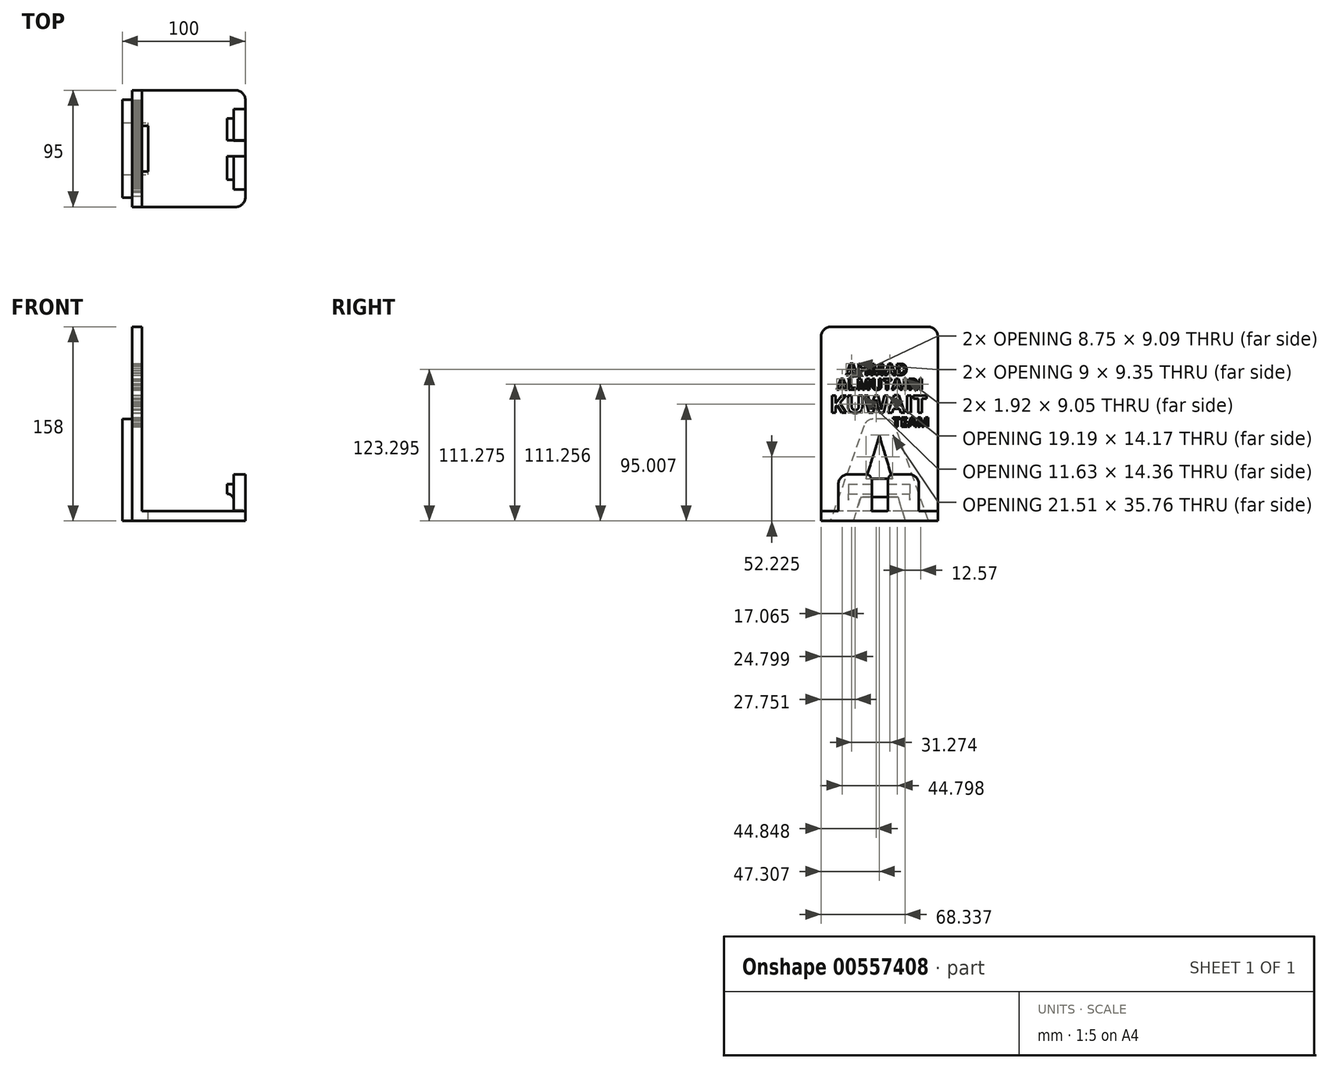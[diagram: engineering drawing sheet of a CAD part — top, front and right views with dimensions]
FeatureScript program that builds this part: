
annotation { "Feature Type Name" : "Feature", "Feature Type Description" : "" }
export const myFeature = defineFeature(function(context is Context, id is Id, definition is map)
    precondition{}
    {
        {
            var Q0;
            Q0=qCreatedBy(makeId("Top.planeOp"),FACE);
            var sketch = newSketch(context, id + "F0", { "sketchPlane" : qUnion([Q0])});
            skLineSegment(sketch, "E0.bottom", {"start": v(-46, -47.5) * mm, "end": v(46, -47.5) * mm});
            skLineSegment(sketch, "E0.top", {"start": v(-46, 47.5) * mm, "end": v(46, 47.5) * mm});
            skLineSegment(sketch, "E0.left", {"start": v(-46, -47.5) * mm, "end": v(-46, 47.5) * mm});
            skLineSegment(sketch, "E0.right", {"start": v(46, -47.5) * mm, "end": v(46, 47.5) * mm});
            skPoint(sketch, "E0.middle", {"position": v(0, 0) * mm});
            skSolve(sketch);
        }
        {
            var Q0;
            Q0=makeQuery(id+"F0.imprint","IMPRINT",FACE,{"disambiguationData":[TD([[makeQuery(id+"F0.imprint","IMPRINT",EDGE,{"derivedFrom":sQuery(id+"F0.wireOp",EDGE,"E0.bottom")}),1.0]])]});
            extrude(context, id + "F1", {"entities" : qUnion([Q0]), "depth" : 8 * mm, "offsetDistance" : 25 * mm});
        }
        {
            var Q0;
            Q0=makeQuery(id+"F1.opExtrude","CAP_FACE",FACE,{"disambiguationData":[OSD([sQuery(id+"F0.wireOp",EDGE,"E0.bottom"),sQuery(id+"F0.wireOp",EDGE,"E0.top"),sQuery(id+"F0.wireOp",EDGE,"E0.left"),sQuery(id+"F0.wireOp",EDGE,"E0.right")])],"isStart":false});
            var sketch = newSketch(context, id + "F2", { "sketchPlane" : qUnion([Q0])});
            skLineSegment(sketch, "E1.bottom", {"start": v(-46, 47.5) * mm, "end": v(-38, 47.5) * mm});
            skLineSegment(sketch, "E1.top", {"start": v(-46, -47.5) * mm, "end": v(-38, -47.5) * mm});
            skLineSegment(sketch, "E1.left", {"start": v(-46, 47.5) * mm, "end": v(-46, -47.5) * mm});
            skLineSegment(sketch, "E1.right", {"start": v(-38, 47.5) * mm, "end": v(-38, -47.5) * mm});
            skSolve(sketch);
        }
        {
            var Q0;
            Q0=qSketchRegion(id+"F2",true);
            extrude(context, id + "F3", {"entities" : qUnion([Q0]), "operationType" : NewBodyOperationType.ADD, "depth" : 150 * mm, "offsetDistance" : 25 * mm});
        }
        {
            var Q0;
            Q0=makeQuery(id+"F1.opExtrude","CAP_FACE",FACE,{"disambiguationData":[OSD([sQuery(id+"F0.wireOp",EDGE,"E0.bottom"),sQuery(id+"F0.wireOp",EDGE,"E0.top"),sQuery(id+"F0.wireOp",EDGE,"E0.left"),sQuery(id+"F0.wireOp",EDGE,"E0.right")])],"isStart":false});
            var sketch = newSketch(context, id + "F4", { "sketchPlane" : qUnion([Q0])});
            skLineSegment(sketch, "E2.bottom", {"start": v(46, 32.06) * mm, "end": v(36.5, 32.06) * mm});
            skLineSegment(sketch, "E2.top", {"start": v(46, -33.37) * mm, "end": v(36.5, -33.37) * mm});
            skLineSegment(sketch, "E2.left", {"start": v(46, 32.06) * mm, "end": v(46, -33.37) * mm});
            skLineSegment(sketch, "E2.right", {"start": v(36.5, 32.06) * mm, "end": v(36.5, -33.37) * mm});
            skSolve(sketch);
        }
        {
            var Q0;
            Q0=makeQuery(id+"F4.imprint","IMPRINT",FACE,{"disambiguationData":[TD([[makeQuery(id+"F4.imprint","IMPRINT",EDGE,{"derivedFrom":sQuery(id+"F4.wireOp",EDGE,"E2.bottom")}),1.0]])]});
            extrude(context, id + "F5", {"entities" : qUnion([Q0]), "operationType" : NewBodyOperationType.ADD, "depth" : 30 * mm, "offsetDistance" : 25 * mm});
        }
        {
            var Q0;
            Q0=makeQuery(id+"F3.boolean.opBoolean","MERGE",FACE,{"derivedFrom":[makeQuery(id+"F1.opExtrude","SWEPT_FACE",FACE,{"disambiguationData":[OSD([sQuery(id+"F0.wireOp",EDGE,"E0.left")])]}),makeQuery(id+"F3.opExtrude","SWEPT_FACE",FACE,{"disambiguationData":[OSD([sQuery(id+"F2.wireOp",EDGE,"E1.left")])]})]});
            var sketch = newSketch(context, id + "F6", { "sketchPlane" : qUnion([Q0])});
            skText(sketch, "E3", { "text": "A", "fontName": "OpenSans-Bold.ttf"});
            const initialGuessF6  = {"E3": [-0.03983, 0, 1, 0, 0.0833]};
            skSetInitialGuess(sketch, initialGuessF6);
            skSolve(sketch);
        }
        {
            var Q0;
            Q0=qSketchRegion(id+"F6",true);
            extrude(context, id + "F7", {"entities" : qUnion([Q0]), "operationType" : NewBodyOperationType.ADD, "depth" : 8 * mm, "offsetDistance" : 25 * mm});
        }
        {
            var Q0;
            Q0=makeQuery(id+"F7.boolean.opBoolean","SPLIT",FACE,{"disambiguationData":[TD([makeQuery(id+"F7.opExtrude","SWEPT_FACE",FACE,{"disambiguationData":[OSD([sQuery(id+"F6.wireOp",EDGE,"E3.sketch_text.stroke-8")])]})])],"derivedFrom":makeQuery(id+"F3.boolean.opBoolean","MERGE",FACE,{"derivedFrom":[makeQuery(id+"F1.opExtrude","SWEPT_FACE",FACE,{"disambiguationData":[OSD([sQuery(id+"F0.wireOp",EDGE,"E0.left")])]}),makeQuery(id+"F3.opExtrude","SWEPT_FACE",FACE,{"disambiguationData":[OSD([sQuery(id+"F2.wireOp",EDGE,"E1.left")])]})]})});
            var Q1;
            {var subQ0=sQuery(id+"F0.wireOp",EDGE,"E0.left");Q1=makeQuery(id+"F7.boolean.opBoolean","SPLIT",FACE,{"disambiguationData":[TD([makeQuery(id+"F7.opExtrude","SWEPT_FACE",FACE,{"disambiguationData":[OSD([sQuery(id+"F6.wireOp",EDGE,"E3.sketch_text.stroke-0")])]})])],"derivedFrom":makeQuery(id+"F3.boolean.opBoolean","MERGE",FACE,{"derivedFrom":[makeQuery(id+"F1.opExtrude","SWEPT_FACE",FACE,{"disambiguationData":[OSD([subQ0])]}),makeQuery(id+"F3.opExtrude","SWEPT_FACE",FACE,{"disambiguationData":[OSD([sQuery(id+"F2.wireOp",EDGE,"E1.left")])]})]})});}
            extrude(context, id + "F8", {"entities" : qUnion([Q0, Q1]), "operationType" : NewBodyOperationType.REMOVE, "oppositeDirection" : true, "depth" : 13 * mm, "offsetDistance" : 25 * mm});
        }
        {
            var Q0;
            Q0=makeQuery(id+"F1.opExtrude","CAP_FACE",FACE,{"disambiguationData":[OSD([sQuery(id+"F0.wireOp",EDGE,"E0.bottom"),sQuery(id+"F0.wireOp",EDGE,"E0.top"),sQuery(id+"F0.wireOp",EDGE,"E0.left"),sQuery(id+"F0.wireOp",EDGE,"E0.right")])],"isStart":false});
            var sketch = newSketch(context, id + "F9", { "sketchPlane" : qUnion([Q0])});
            skLineSegment(sketch, "E4.bottom", {"start": v(-46.36, -6.41) * mm, "end": v(46.36, -6.41) * mm});
            skLineSegment(sketch, "E4.top", {"start": v(-46.36, 6.41) * mm, "end": v(46.36, 6.41) * mm});
            skLineSegment(sketch, "E4.left", {"start": v(-46.36, -6.41) * mm, "end": v(-46.36, 6.41) * mm});
            skLineSegment(sketch, "E4.right", {"start": v(46.36, -6.41) * mm, "end": v(46.36, 6.41) * mm});
            skPoint(sketch, "E4.middle", {"position": v(0, 0) * mm});
            skSolve(sketch);
        }
        {
            var Q0;
            Q0=qSketchRegion(id+"F9",true);
            extrude(context, id + "F10", {"entities" : qUnion([Q0]), "operationType" : NewBodyOperationType.REMOVE, "depth" : 8 * mm, "offsetDistance" : 25 * mm});
        }
        {
            var Q0;
            Q0=makeQuery(id+"F5.opExtrude","CAP_EDGE",EDGE,{"disambiguationData":[OSD([sQuery(id+"F4.wireOp",EDGE,"E2.top")])],"isStart":false});
            var Q1;
            Q1=makeQuery(id+"F10.boolean.opBoolean","COPY",EDGE,{"derivedFrom":makeQuery(id+"F10.opExtrude","CAP_EDGE",EDGE,{"disambiguationData":[OSD([sQuery(id+"F9.wireOp",EDGE,"E4.bottom")])],"isStart":false})});
            var Q2;
            Q2=makeQuery(id+"F5.opExtrude","CAP_EDGE",EDGE,{"disambiguationData":[OSD([sQuery(id+"F4.wireOp",EDGE,"E2.bottom")])],"isStart":false});
            var Q3;
            Q3=makeQuery(id+"F10.boolean.opBoolean","COPY",EDGE,{"derivedFrom":makeQuery(id+"F10.opExtrude","CAP_EDGE",EDGE,{"disambiguationData":[OSD([sQuery(id+"F9.wireOp",EDGE,"E4.top")])],"isStart":false})});
            var Q4;
            Q4=makeQuery(id+"F1.opExtrude","SWEPT_EDGE",EDGE,{"disambiguationData":[OSD([sQuery(id+"F0.wireOp",EDGE,"E0.bottom"),sQuery(id+"F0.wireOp",EDGE,"E0.right")])]});
            var Q5;
            Q5=makeQuery(id+"F1.opExtrude","SWEPT_EDGE",EDGE,{"disambiguationData":[OSD([sQuery(id+"F0.wireOp",EDGE,"E0.top"),sQuery(id+"F0.wireOp",EDGE,"E0.right")])]});
            var Q6;
            Q6=makeQuery(id+"F3.opExtrude","CAP_EDGE",EDGE,{"disambiguationData":[OSD([sQuery(id+"F2.wireOp",EDGE,"E1.bottom")])],"isStart":false});
            var Q7;
            Q7=makeQuery(id+"F3.opExtrude","CAP_EDGE",EDGE,{"disambiguationData":[OSD([sQuery(id+"F2.wireOp",EDGE,"E1.top")])],"isStart":false});
            var Q8;
            Q8=makeQuery(id+"F7.opExtrude","SWEPT_EDGE",EDGE,{"disambiguationData":[OSD([sQuery(id+"F6.wireOp",EDGE,"E3.sketch_text.stroke-5"),sQuery(id+"F6.wireOp",EDGE,"E3.sketch_text.stroke-6")])]});
            var Q9;
            Q9=makeQuery(id+"F7.opExtrude","SWEPT_EDGE",EDGE,{"disambiguationData":[OSD([sQuery(id+"F6.wireOp",EDGE,"E3.sketch_text.stroke-4"),sQuery(id+"F6.wireOp",EDGE,"E3.sketch_text.stroke-5")])]});
            fillet(context, id + "F11", {"entities" : qUnion([Q0, Q1, Q2, Q3, Q4, Q5, Q6, Q7, Q8, Q9]), "radius" : 8 * mm, "tangentPropagation" : true, "allowEdgeOverflow" : false});
        }
        {
            var Q0;
            Q0=makeQuery(id+"F3.opExtrude","SWEPT_FACE",FACE,{"disambiguationData":[OSD([sQuery(id+"F2.wireOp",EDGE,"E1.right")])]});
            var sketch = newSketch(context, id + "F12", { "sketchPlane" : qUnion([Q0])});
            skSolve(sketch);
        }
        {
            var Q0;
            Q0=makeQuery(id+"F5.boolean.opBoolean","MERGE",FACE,{"derivedFrom":[makeQuery(id+"F1.opExtrude","SWEPT_FACE",FACE,{"disambiguationData":[OSD([sQuery(id+"F0.wireOp",EDGE,"E0.right")])]}),makeQuery(id+"F5.opExtrude","SWEPT_FACE",FACE,{"disambiguationData":[OSD([sQuery(id+"F4.wireOp",EDGE,"E2.left")])]})]});
            var sketch = newSketch(context, id + "F13", { "sketchPlane" : qUnion([Q0])});
            skLineSegment(sketch, "E5.bottom", {"start": v(-25.37, 30) * mm, "end": v(24.63, 30) * mm});
            skLineSegment(sketch, "E5.top", {"start": v(-25.37, 22) * mm, "end": v(24.63, 22) * mm});
            skLineSegment(sketch, "E5.left", {"start": v(-25.37, 30) * mm, "end": v(-25.37, 22) * mm});
            skLineSegment(sketch, "E5.right", {"start": v(24.63, 30) * mm, "end": v(24.63, 22) * mm});
            skSolve(sketch);
        }
        {
            var Q0;
            Q0=qSketchRegion(id+"F13",true);
            extrude(context, id + "F14", {"entities" : qUnion([Q0]), "operationType" : NewBodyOperationType.ADD, "oppositeDirection" : true, "depth" : 15 * mm, "offsetDistance" : 25 * mm});
        }
        {
            var Q0;
            Q0=qCreatedBy(makeId("Right.planeOp"),FACE);
            var sketch = newSketch(context, id + "F15", { "sketchPlane" : qUnion([Q0])});
            skLineSegment(sketch, "E6.bottom", {"start": v(-6.29, 8.45) * mm, "end": v(6.71, 8.45) * mm});
            skLineSegment(sketch, "E6.top", {"start": v(-6.29, 38.45) * mm, "end": v(6.71, 38.45) * mm});
            skLineSegment(sketch, "E6.left", {"start": v(-6.29, 8.45) * mm, "end": v(-6.29, 38.45) * mm});
            skLineSegment(sketch, "E6.right", {"start": v(6.71, 8.45) * mm, "end": v(6.71, 38.45) * mm});
            skSolve(sketch);
        }
        {
            var Q0;
            Q0=qSketchRegion(id+"F15",true);
            extrude(context, id + "F16", {"entities" : qUnion([Q0]), "operationType" : NewBodyOperationType.REMOVE, "depth" : 51 * mm, "offsetDistance" : 25 * mm});
        }
        {
            var Q0;
            Q0=makeQuery(id+"F16.boolean.opBoolean","INTERSECT",EDGE,{"derivedFrom":[makeQuery(id+"F5.opExtrude","CAP_FACE",FACE,{"disambiguationData":[OSD([sQuery(id+"F4.wireOp",EDGE,"E2.bottom"),sQuery(id+"F4.wireOp",EDGE,"E2.top"),sQuery(id+"F4.wireOp",EDGE,"E2.left"),sQuery(id+"F4.wireOp",EDGE,"E2.right")])],"isStart":false}),makeQuery(id+"F16.opExtrude","SWEPT_FACE",FACE,{"disambiguationData":[OSD([sQuery(id+"F15.wireOp",EDGE,"E6.left")])]})]});
            var Q1;
            Q1=makeQuery(id+"F16.boolean.opBoolean","INTERSECT",EDGE,{"derivedFrom":[makeQuery(id+"F5.opExtrude","CAP_FACE",FACE,{"disambiguationData":[OSD([sQuery(id+"F4.wireOp",EDGE,"E2.bottom"),sQuery(id+"F4.wireOp",EDGE,"E2.top"),sQuery(id+"F4.wireOp",EDGE,"E2.left"),sQuery(id+"F4.wireOp",EDGE,"E2.right")])],"isStart":false}),makeQuery(id+"F16.opExtrude","SWEPT_FACE",FACE,{"disambiguationData":[OSD([sQuery(id+"F15.wireOp",EDGE,"E6.right")])]})]});
            fillet(context, id + "F17", {"entities" : qUnion([Q0, Q1]), "radius" : 5 * mm, "tangentPropagation" : true, "allowEdgeOverflow" : false});
        }
        {
            var Q0;
            {var subQ0=sQuery(id+"F2.wireOp",EDGE,"E1.right");Q0=makeQuery(id+"F12.imprint","IMPRINT",FACE,{"disambiguationData":[TD([[makeQuery(id+"F12.imprint","IMPRINT",EDGE,{"derivedFrom":makeQuery(id+"F3.opExtrude","CAP_EDGE",EDGE,{"disambiguationData":[OSD([subQ0])],"isStart":false})}),1.0]])]});}
            var sketch = newSketch(context, id + "F18", { "sketchPlane" : qUnion([Q0])});
            skText(sketch, "E7", { "text": "KUWAIT", "fontName": "OpenSans-Bold.ttf"});
            const initialGuessF18  = {"E7": [-0.04043, 0.08802, 1, 0, 0.01429]};
            skSetInitialGuess(sketch, initialGuessF18);
            skSolve(sketch);
        }
        {
            var Q0;
            {var subQ0=sQuery(id+"F2.wireOp",EDGE,"E1.right");Q0=makeQuery(id+"F12.imprint","IMPRINT",FACE,{"disambiguationData":[TD([[makeQuery(id+"F12.imprint","IMPRINT",EDGE,{"derivedFrom":makeQuery(id+"F3.opExtrude","CAP_EDGE",EDGE,{"disambiguationData":[OSD([subQ0])],"isStart":false})}),1.0]])]});}
            var sketch = newSketch(context, id + "F19", { "sketchPlane" : qUnion([Q0])});
            skText(sketch, "E8", { "text": "TEAM", "fontName": "OpenSans-Bold.ttf"});
            const initialGuessF19  = {"E8": [0.01073, 0.07663, 1, 0, 0.00774]};
            skSetInitialGuess(sketch, initialGuessF19);
            skSolve(sketch);
        }
        {
            var Q0;
            {var subQ0=sQuery(id+"F2.wireOp",EDGE,"E1.right");Q0=makeQuery(id+"F12.imprint","IMPRINT",FACE,{"disambiguationData":[TD([[makeQuery(id+"F12.imprint","IMPRINT",EDGE,{"derivedFrom":makeQuery(id+"F3.opExtrude","CAP_EDGE",EDGE,{"disambiguationData":[OSD([subQ0])],"isStart":false})}),1.0]])]});}
            var sketch = newSketch(context, id + "F20", { "sketchPlane" : qUnion([Q0])});
            skText(sketch, "E9", { "text": "AHMAD\n", "fontName": "OpenSans-Bold.ttf"});
            const initialGuessF20  = {"E9": [-0.0272, 0.11862, 1, 0, 0.00939]};
            skSetInitialGuess(sketch, initialGuessF20);
            skSolve(sketch);
        }
        {
            var Q0;
            {var subQ0=sQuery(id+"F2.wireOp",EDGE,"E1.right");Q0=makeQuery(id+"F12.imprint","IMPRINT",FACE,{"disambiguationData":[TD([[makeQuery(id+"F12.imprint","IMPRINT",EDGE,{"derivedFrom":makeQuery(id+"F3.opExtrude","CAP_EDGE",EDGE,{"disambiguationData":[OSD([subQ0])],"isStart":false})}),1.0]])]});}
            var sketch = newSketch(context, id + "F21", { "sketchPlane" : qUnion([Q0])});
            skText(sketch, "E10", { "text": "ALMUTAIRI", "fontName": "OpenSans-Bold.ttf"});
            const initialGuessF21  = {"E10": [-0.03481, 0.10673, 1, 0, 0.00913]};
            skSetInitialGuess(sketch, initialGuessF21);
            skSolve(sketch);
        }
        {
            var Q0;
            Q0=qSketchRegion(id+"F21",true);
            var Q1;
            Q1=qSketchRegion(id+"F18",true);
            var Q2;
            Q2=qSketchRegion(id+"F19",true);
            var Q3;
            Q3=qSketchRegion(id+"F20",true);
            extrude(context, id + "F22", {"entities" : qUnion([Q0, Q1, Q2, Q3]), "operationType" : NewBodyOperationType.REMOVE, "oppositeDirection" : true, "depth" : 25 * mm, "offsetDistance" : 25 * mm});
        }
        {
            var Q0;
            {var subQ0=makeQuery(id+"F5.opExtrude","SWEPT_FACE",FACE,{"disambiguationData":[OSD([sQuery(id+"F4.wireOp",EDGE,"E2.right")])]});var subQ1=makeQuery(id+"F14.opExtrude","SWEPT_FACE",FACE,{"disambiguationData":[OSD([sQuery(id+"F13.wireOp",EDGE,"E5.top")])]});Q0=makeQuery(id+"F16.boolean.opBoolean","SPLIT",EDGE,{"disambiguationData":[TD([makeQuery(id+"F14.opExtrude","SWEPT_FACE",FACE,{"disambiguationData":[OSD([sQuery(id+"F13.wireOp",EDGE,"E5.right")])]})])],"derivedFrom":makeQuery(id+"F14.boolean.opBoolean","INTERSECT",EDGE,{"derivedFrom":[subQ0,subQ1]})});}
            var Q1;
            {var subQ0=makeQuery(id+"F5.opExtrude","SWEPT_FACE",FACE,{"disambiguationData":[OSD([sQuery(id+"F4.wireOp",EDGE,"E2.right")])]});var subQ1=makeQuery(id+"F14.opExtrude","SWEPT_FACE",FACE,{"disambiguationData":[OSD([sQuery(id+"F13.wireOp",EDGE,"E5.top")])]});Q1=makeQuery(id+"F16.boolean.opBoolean","SPLIT",EDGE,{"disambiguationData":[TD([makeQuery(id+"F14.opExtrude","SWEPT_FACE",FACE,{"disambiguationData":[OSD([sQuery(id+"F13.wireOp",EDGE,"E5.left")])]})])],"derivedFrom":makeQuery(id+"F14.boolean.opBoolean","INTERSECT",EDGE,{"derivedFrom":[subQ0,subQ1]})});}
            fillet(context, id + "F23", {"entities" : qUnion([Q0, Q1]), "radius" : 5 * mm, "tangentPropagation" : true, "allowEdgeOverflow" : false});
        }
    });
